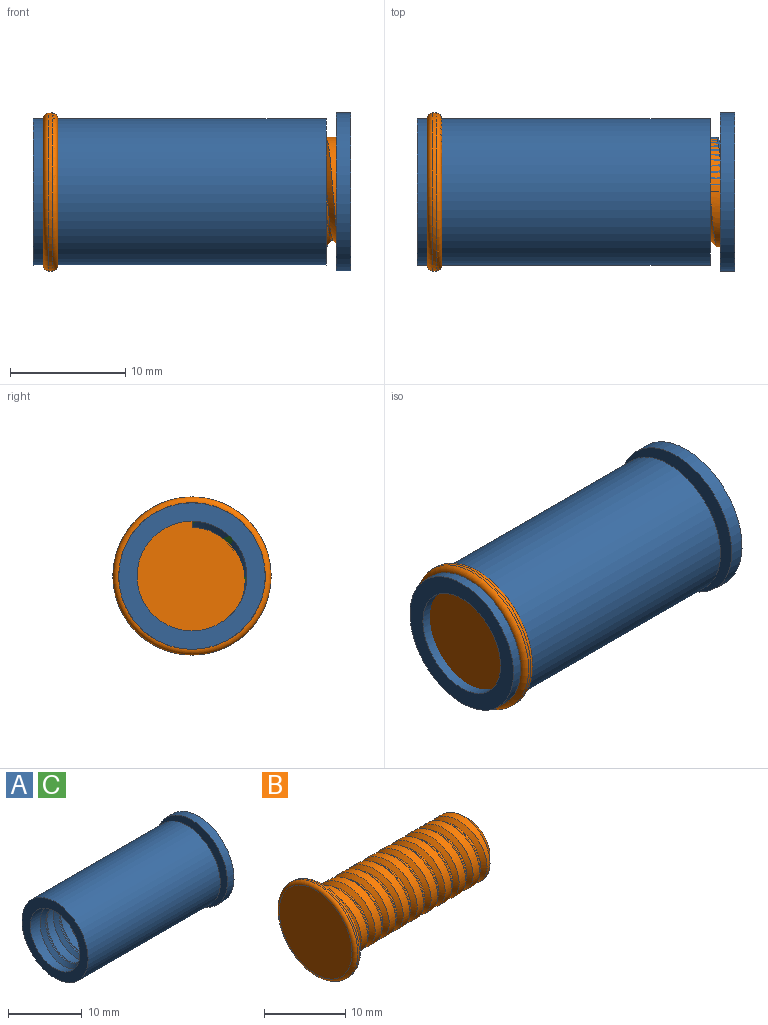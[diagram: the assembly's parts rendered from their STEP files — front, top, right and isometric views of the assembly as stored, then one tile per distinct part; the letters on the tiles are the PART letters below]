
ASSEMBLY  parts=3 mates=1
PART A: 13 faces, bbox 27.7x13.9x13.9 mm
  f0: cylinder r=4.76mm len=9.53mm, axis (-1,0,0), area 8.8mm2, adj f1,f2,f6,f10
  f1: plane 0.85x0.55mm, normal (0,-1,0), area 0.3mm2, adj f0,f2,f8,f9,f10
  f2: bspline ~25.95x11mm, area 217.7mm2, adj f0,f1,f3,f7,f8,f10
  f3: cylinder r=4.76mm len=25.4mm, axis (-1,0,0), area 414mm2, adj f2,f5,f6,f7,f9
  f4: cylinder r=6.35mm len=25.4mm, axis (-1,0,0), area 1013.4mm2, adj f5,f6
  f5: plane 12.7x12.7mm, normal (-1,0,0), area 55.4mm2, adj f3,f4
  f6: plane 12.7x12.7mm, normal (1,0,0), area 55.4mm2, adj f0,f3,f4
  f7: plane 1.3x0.55mm, normal (0,1,0), area 0.4mm2, adj f2,f3,f8,f9
  f8: cylinder r=4.21mm len=25.6mm, axis (-1,0,0), area 52.9mm2, adj f1,f2,f7,f9
  f9: bspline ~25.95x11mm, area 219.3mm2, adj f1,f3,f7,f8
  f10: plane 13.85x13.85mm, normal (-1,0,0), area 146.6mm2, adj f0,f1,f2,f12
  f11: plane 13.72x13.72mm, normal (1,0,0), area 147.8mm2, adj f12
  f12: cylinder r=6.86mm len=13.72mm, axis (-1,0,0), area 54.7mm2, adj f10,f11
PART B: 15 faces, bbox 27x14.8x14.8 mm
  f0: plane 12.72x12.72mm, normal (1,0,0), area 57.2mm2, adj f6,f13
  f1: cylinder r=6.86mm len=13.72mm, axis (1,0,0), area 11.6mm2, adj f13,f14
  f2: plane 12.72x12.72mm, normal (-1,0,0), area 127mm2, adj f14
  f3: cylinder r=4.21mm len=8.43mm, axis (1,0,0), area 7.5mm2, adj f4,f6,f9
  f4: torus R=4.71mm, axis (1,0,0), area 16.5mm2, adj f3,f5,f9,f10,f11
  f5: plane 9.46x5.39mm, normal (-1,0,0), area 0.7mm2, adj f4,f10,f11,f12
  f6: torus R=4.71mm, axis (1,0,0), area 21.7mm2, adj f0,f3
  f7: plane 7.53x7.53mm, normal (1,0,0), area 44.5mm2, adj f8
  f8: cone r=3.76mm half-angle=45deg, axis (-1,0,0), area 31mm2, adj f7,f9,f10,f11,f12
  f9: cylinder r=4.21mm len=24.4mm, axis (-1,0,0), area 65.9mm2, adj f3,f4,f8,f10,f11
  f10: bspline ~24.95x11mm, area 212.3mm2, adj f4,f5,f8,f9,f12
  f11: bspline ~24.95x11mm, area 211.8mm2, adj f4,f5,f8,f9,f12
  f12: cylinder r=4.76mm len=23.1mm, axis (1,0,0), area 321.9mm2, adj f5,f8,f10,f11
  f13: torus R=6.36mm, axis (-1,0,0), area 32.9mm2, adj f0,f1
  f14: torus R=6.36mm, axis (1,0,0), area 32.9mm2, adj f1,f2
PART C: same geometry as A
PLACE A t=(14.75,12.11,-3.98)mm
PLACE B t=(15.61,12.11,-3.98)mm
PLACE C t=(14.75,12.11,-3.98)mm
MATE cylindrical B.f1 <-> A.f0  axis (1,0,0) through (42.28,12.11,-3.98)mm
